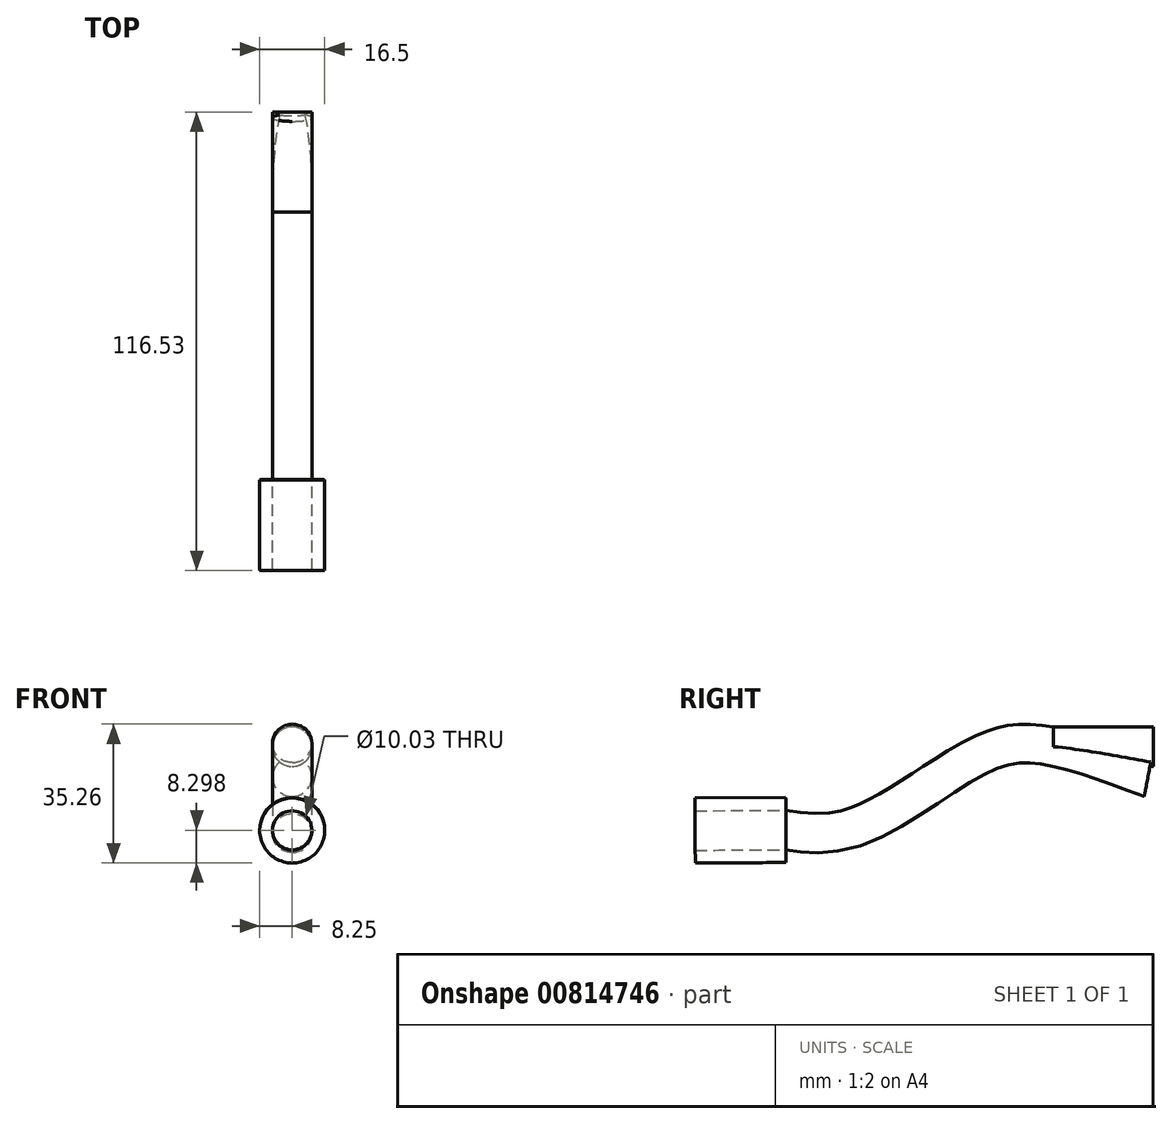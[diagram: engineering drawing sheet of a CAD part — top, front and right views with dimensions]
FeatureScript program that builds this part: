
annotation { "Feature Type Name" : "Feature", "Feature Type Description" : "" }
export const myFeature = defineFeature(function(context is Context, id is Id, definition is map)
    precondition{}
    {
        {
            var Q0;
            Q0=qCreatedBy(makeId("Front.planeOp"),FACE);
            var sketch = newSketch(context, id + "F0", { "sketchPlane" : qUnion([Q0])});
            skCircle(sketch, "E0", {"center": v(0, 0) * mm, "radius": 5.02 * mm});
            skSolve(sketch);
        }
        {
            var Q0;
            Q0=makeQuery(id+"F0.imprint","IMPRINT",FACE,{"disambiguationData":[TD([[makeQuery(id+"F0.imprint","IMPRINT",EDGE,{"derivedFrom":sQuery(id+"F0.wireOp",EDGE,"E0")}),1.0]])]});
            var Q1;
            Q1=sQuery(id+"F0.wireOp",EDGE,"E0");
            extrude(context, id + "F1", {"entities" : qUnion([Q0]), "surfaceEntities" : qUnion([Q1]), "depth" : 25.4 * mm, "offsetDistance" : 25.4 * mm});
        }
        {
            var Q0;
            Q0=qCreatedBy(makeId("Right.planeOp"),FACE);
            var sketch = newSketch(context, id + "F2", { "sketchPlane" : qUnion([Q0])});
            skFitSpline(sketch, "E1", {"points": [v(0, 0) * mm, v(-33.56, 8.48) * mm, v(-55.94, 0) * mm, v(-79.4, -13.35) * mm, v(-93.47, -13.35) * mm], "startDerivative": vector(-119.22, 44.23) * mm, "endDerivative": vector(-70.32, 11.68) * mm});
            skSolve(sketch);
        }
        {
            var Q0;
            Q0=makeQuery(id+"F1.opExtrude","CAP_FACE",FACE,{"disambiguationData":[OSD([sQuery(id+"F0.wireOp",EDGE,"E0")])],"isStart":false});
            var Q1;
            Q1=sQuery(id+"F2.wireOp",EDGE,"E1");
            sweep(context, id + "F3", {"operationType" : NewBodyOperationType.ADD, "profiles" : qUnion([Q0]), "path" : qUnion([Q1])});
        }
        {
            var Q0;
            Q0=makeQuery(id+"F3.opSweep","CAP_FACE",FACE,{"disambiguationData":[OSD([sQuery(id+"F0.wireOp",EDGE,"E0"),sQuery(id+"F2.wireOp",VERTEX,"E1.end")])],"isStart":false});
            var sketch = newSketch(context, id + "F4", { "sketchPlane" : qUnion([Q0])});
            skCircle(sketch, "E2", {"center": v(0, -20.76) * mm, "radius": 8.25 * mm});
            skSolve(sketch);
        }
        {
            var Q0;
            Q0=makeQuery(id+"F4.imprint","IMPRINT",FACE,{"disambiguationData":[TD([[makeQuery(id+"F4.imprint","IMPRINT",EDGE,{"derivedFrom":sQuery(id+"F4.wireOp",EDGE,"E2")}),1.0]])]});
            extrude(context, id + "F5", {"entities" : qUnion([Q0]), "depth" : 23.05 * mm, "offsetDistance" : 25.4 * mm});
        }
    });
